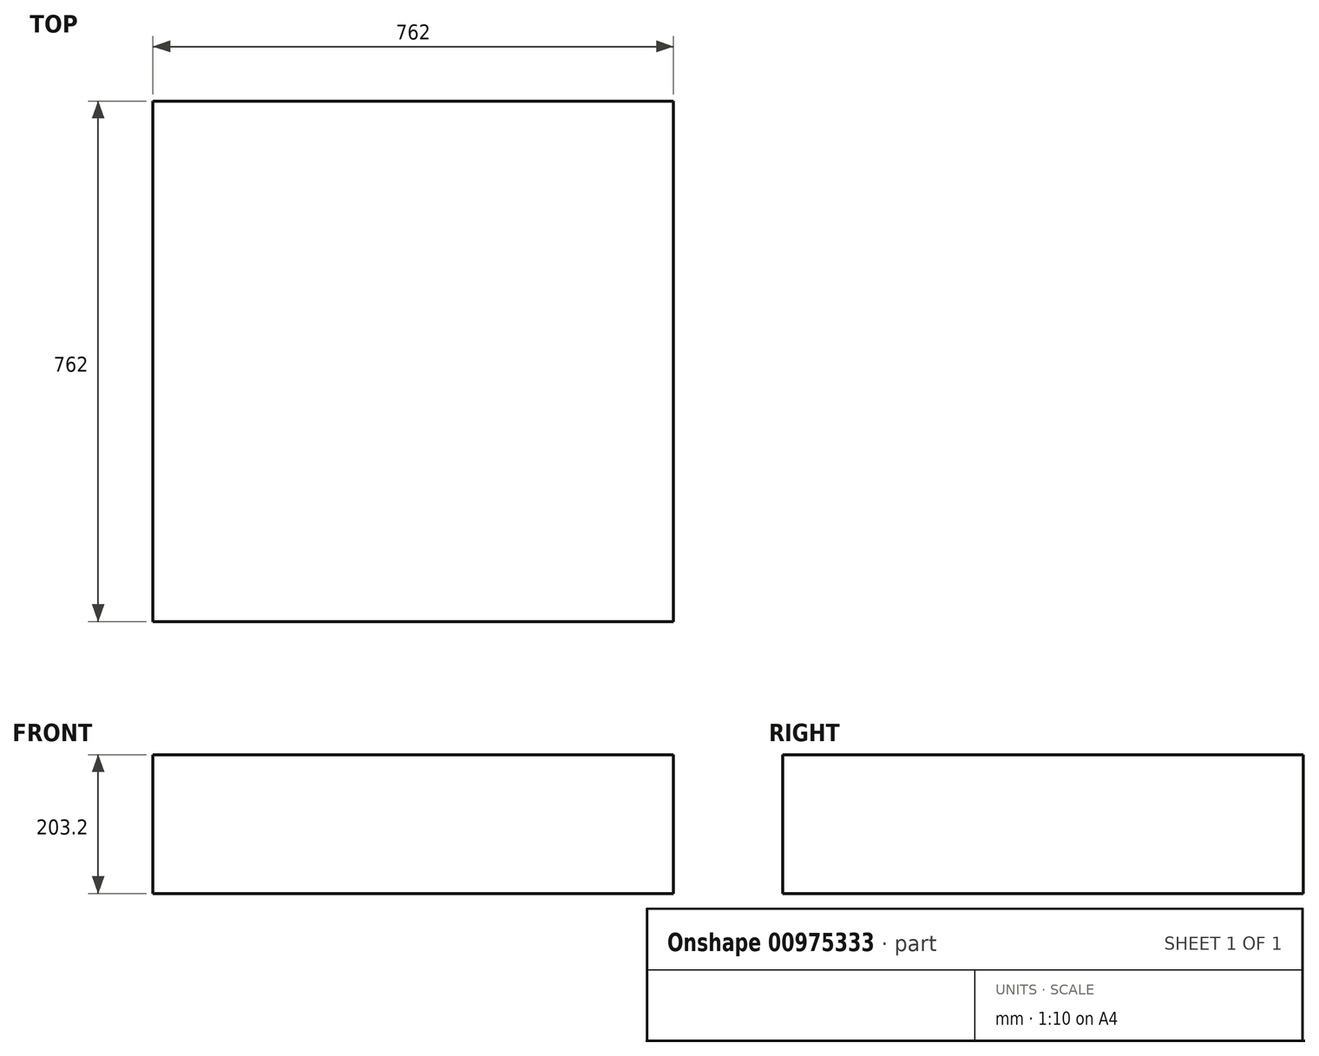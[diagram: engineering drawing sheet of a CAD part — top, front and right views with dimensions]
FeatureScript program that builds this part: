
annotation { "Feature Type Name" : "Feature", "Feature Type Description" : "" }
export const myFeature = defineFeature(function(context is Context, id is Id, definition is map)
    precondition{}
    {
        {
            var Q0;
            Q0=qCreatedBy(makeId("Top.planeOp"),FACE);
            var sketch = newSketch(context, id + "F0", { "sketchPlane" : qUnion([Q0])});
            skLineSegment(sketch, "E0.bottom", {"start": v(-447.32, 518.28) * mm, "end": v(314.68, 518.28) * mm});
            skLineSegment(sketch, "E0.top", {"start": v(-447.32, -243.72) * mm, "end": v(314.68, -243.72) * mm});
            skLineSegment(sketch, "E0.left", {"start": v(-447.32, 518.28) * mm, "end": v(-447.32, -243.72) * mm});
            skLineSegment(sketch, "E0.right", {"start": v(314.68, 518.28) * mm, "end": v(314.68, -243.72) * mm});
            skSolve(sketch);
        }
        {
            var Q0;
            Q0 = qSketchRegion(id + "F0", true);
            extrude(context, id + "F1", {"entities" : qUnion([Q0]), "depth" : 203.2 * mm, "offsetDistance" : 25.4 * mm});
        }
    });
